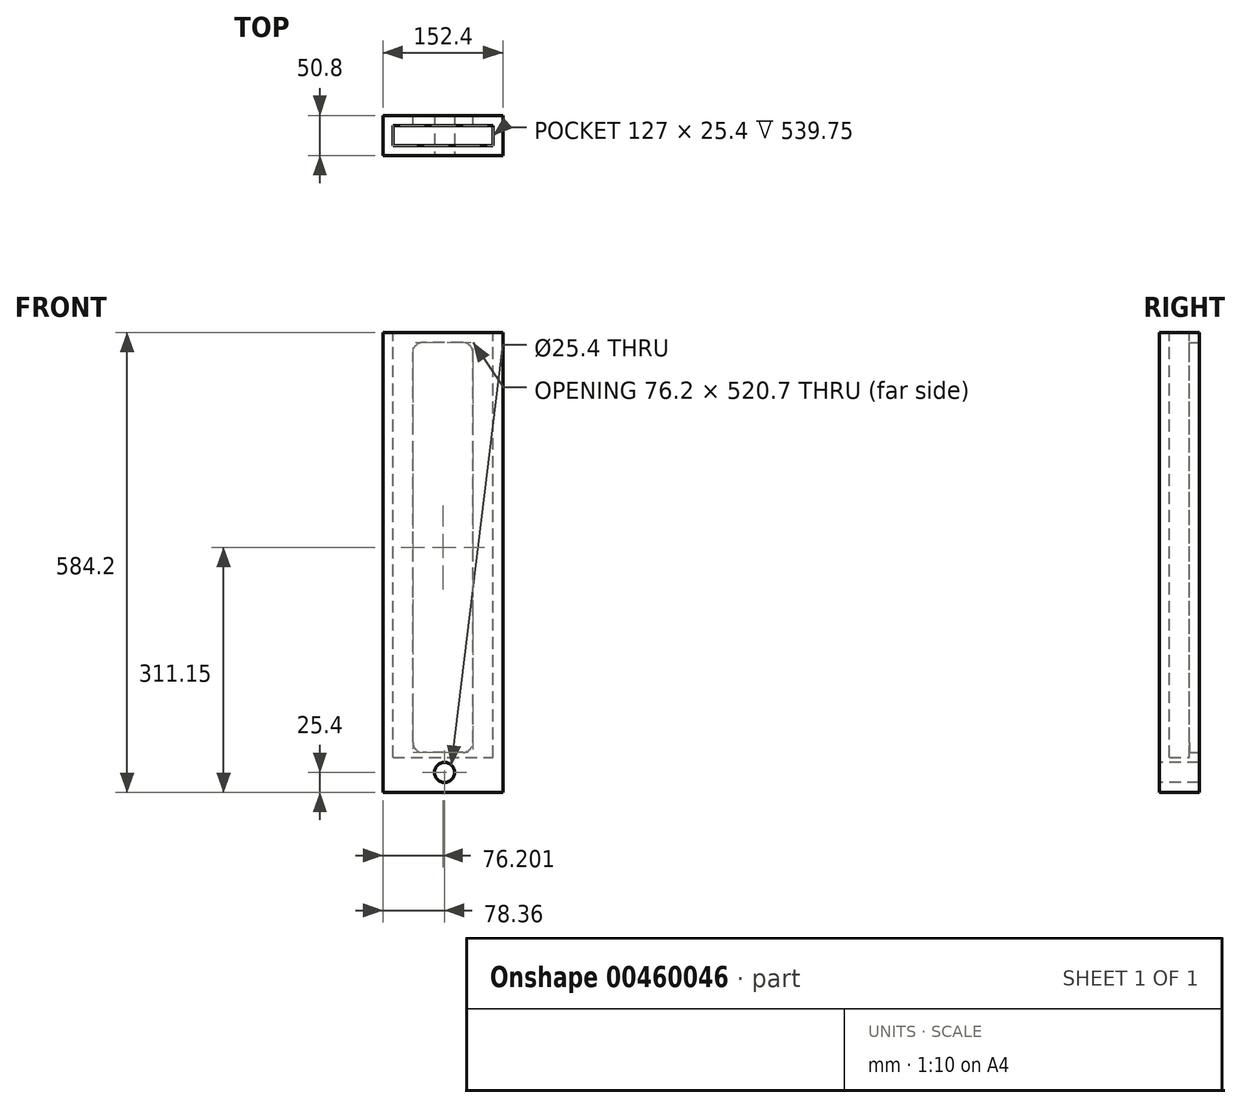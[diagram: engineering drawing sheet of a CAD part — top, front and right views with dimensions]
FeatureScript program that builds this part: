
annotation { "Feature Type Name" : "Feature", "Feature Type Description" : "" }
export const myFeature = defineFeature(function(context is Context, id is Id, definition is map)
    precondition{}
    {
        {
            var Q0;
            Q0=qCreatedBy(makeId("Top.planeOp"),FACE);
            var sketch = newSketch(context, id + "F0", { "sketchPlane" : qUnion([Q0])});
            skLineSegment(sketch, "E0.bottom", {"start": v(-78.36, 30.4) * mm, "end": v(74.04, 30.4) * mm});
            skLineSegment(sketch, "E0.top", {"start": v(-78.36, -20.4) * mm, "end": v(74.04, -20.4) * mm});
            skLineSegment(sketch, "E0.left", {"start": v(-78.36, 30.4) * mm, "end": v(-78.36, -20.4) * mm});
            skLineSegment(sketch, "E0.right", {"start": v(74.04, 30.4) * mm, "end": v(74.04, -20.4) * mm});
            skSolve(sketch);
        }
        {
            var Q0;
            Q0 = qSketchRegion(id + "F0", true);
            extrude(context, id + "F1", {"entities" : qUnion([Q0]), "depth" : 584.2 * mm});
        }
        {
            var Q0;
            Q0=makeQuery(id+"F1.opExtrude","SWEPT_FACE",FACE,{"disambiguationData":[OSD([sQuery(id+"F0.wireOp",EDGE,"E0.top")])]});
            var sketch = newSketch(context, id + "F2", { "sketchPlane" : qUnion([Q0])});
            skCircle(sketch, "E1", {"center": v(0, 25.4) * mm, "radius": 12.7 * mm});
            skSolve(sketch);
        }
        {
            var Q0;
            Q0 = qSketchRegion(id + "F2", true);
            extrude(context, id + "F3", {"entities" : qUnion([Q0]), "operationType" : NewBodyOperationType.REMOVE, "endBound" : BoundingType.THROUGH_ALL, "oppositeDirection" : true, "depth" : 6.35 * mm});
        }
        {
            var Q0;
            Q0=makeQuery(id+"F1.opExtrude","SWEPT_FACE",FACE,{"disambiguationData":[OSD([sQuery(id+"F0.wireOp",EDGE,"E0.bottom")])]});
            var sketch = newSketch(context, id + "F4", { "sketchPlane" : qUnion([Q0])});
            skLineSegment(sketch, "E2.bottom", {"start": v(-35.94, 50.8) * mm, "end": v(40.26, 50.8) * mm});
            skLineSegment(sketch, "E2.top", {"start": v(-35.94, 571.5) * mm, "end": v(40.26, 571.5) * mm});
            skLineSegment(sketch, "E2.left", {"start": v(-35.94, 50.8) * mm, "end": v(-35.94, 571.5) * mm});
            skLineSegment(sketch, "E2.right", {"start": v(40.26, 50.8) * mm, "end": v(40.26, 571.5) * mm});
            skSolve(sketch);
        }
        {
            var Q0;
            Q0=makeQuery(id+"F4.imprint","IMPRINT",FACE,{"disambiguationData":[TD([[makeQuery(id+"F4.imprint","IMPRINT",EDGE,{"derivedFrom":sQuery(id+"F4.wireOp",EDGE,"E2.bottom")}),1.0]])]});
            extrude(context, id + "F5", {"entities" : qUnion([Q0]), "operationType" : NewBodyOperationType.REMOVE, "oppositeDirection" : true, "depth" : 25.4 * mm});
        }
        {
            var Q0;
            Q0=makeQuery(id+"F5.boolean.opBoolean","COPY",EDGE,{"derivedFrom":makeQuery(id+"F5.opExtrude","SWEPT_EDGE",EDGE,{"disambiguationData":[OSD([sQuery(id+"F4.wireOp",EDGE,"E2.bottom"),sQuery(id+"F4.wireOp",EDGE,"E2.left")])]})});
            var Q1;
            Q1=makeQuery(id+"F5.boolean.opBoolean","COPY",EDGE,{"derivedFrom":makeQuery(id+"F5.opExtrude","SWEPT_EDGE",EDGE,{"disambiguationData":[OSD([sQuery(id+"F4.wireOp",EDGE,"E2.bottom"),sQuery(id+"F4.wireOp",EDGE,"E2.right")])]})});
            var Q2;
            Q2=makeQuery(id+"F5.boolean.opBoolean","COPY",EDGE,{"derivedFrom":makeQuery(id+"F5.opExtrude","SWEPT_EDGE",EDGE,{"disambiguationData":[OSD([sQuery(id+"F4.wireOp",EDGE,"E2.top"),sQuery(id+"F4.wireOp",EDGE,"E2.right")])]})});
            var Q3;
            Q3=makeQuery(id+"F5.boolean.opBoolean","COPY",EDGE,{"derivedFrom":makeQuery(id+"F5.opExtrude","SWEPT_EDGE",EDGE,{"disambiguationData":[OSD([sQuery(id+"F4.wireOp",EDGE,"E2.top"),sQuery(id+"F4.wireOp",EDGE,"E2.left")])]})});
            fillet(context, id + "F6", {"entities" : qUnion([Q0, Q1, Q2, Q3]), "radius" : 12.7 * mm, "tangentPropagation" : true, "allowEdgeOverflow" : false});
        }
        {
            var Q0;
            Q0=makeQuery(id+"F1.opExtrude","CAP_FACE",FACE,{"disambiguationData":[OSD([sQuery(id+"F0.wireOp",EDGE,"E0.bottom"),sQuery(id+"F0.wireOp",EDGE,"E0.top"),sQuery(id+"F0.wireOp",EDGE,"E0.left"),sQuery(id+"F0.wireOp",EDGE,"E0.right")])],"isStart":false});
            var sketch = newSketch(context, id + "F7", { "sketchPlane" : qUnion([Q0])});
            skLineSegment(sketch, "E3.bottom", {"start": v(-65.66, -7.7) * mm, "end": v(61.34, -7.7) * mm});
            skLineSegment(sketch, "E3.top", {"start": v(-65.66, 17.7) * mm, "end": v(61.34, 17.7) * mm});
            skLineSegment(sketch, "E3.left", {"start": v(-65.66, -7.7) * mm, "end": v(-65.66, 17.7) * mm});
            skLineSegment(sketch, "E3.right", {"start": v(61.34, -7.7) * mm, "end": v(61.34, 17.7) * mm});
            skSolve(sketch);
        }
        {
            var Q0;
            Q0=makeQuery(id+"F7.imprint","IMPRINT",FACE,{"disambiguationData":[TD([[makeQuery(id+"F7.imprint","IMPRINT",EDGE,{"derivedFrom":sQuery(id+"F7.wireOp",EDGE,"E3.bottom")}),1.0]])]});
            extrude(context, id + "F8", {"entities" : qUnion([Q0]), "operationType" : NewBodyOperationType.REMOVE, "oppositeDirection" : true, "depth" : 539.75 * mm});
        }
    });
